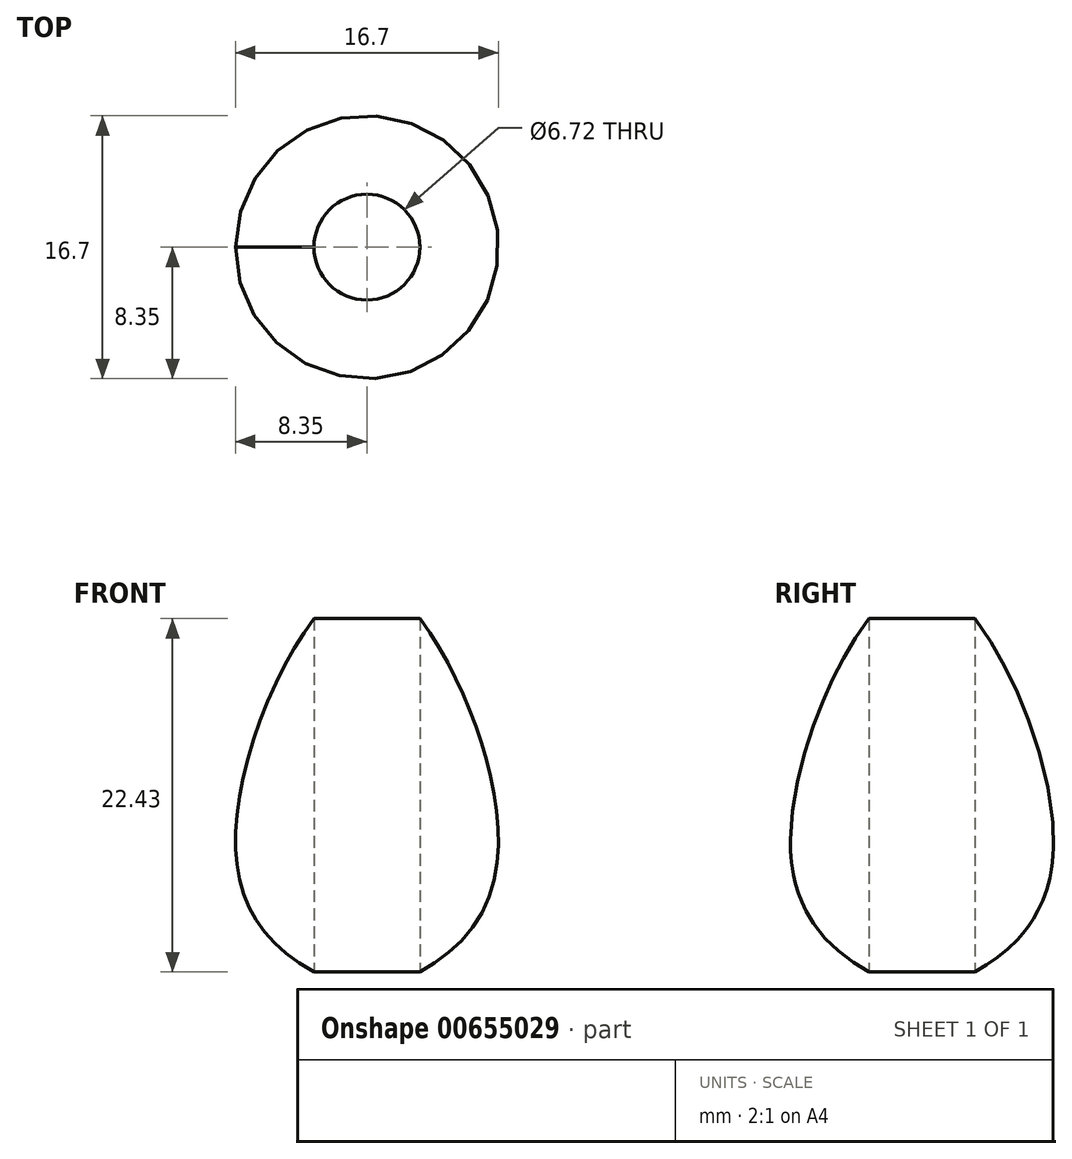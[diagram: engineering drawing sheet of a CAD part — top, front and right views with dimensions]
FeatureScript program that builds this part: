
annotation { "Feature Type Name" : "Feature", "Feature Type Description" : "" }
export const myFeature = defineFeature(function(context is Context, id is Id, definition is map)
    precondition{}
    {
        {
            var Q0;
            Q0=qCreatedBy(makeId("Front.planeOp"),FACE);
            var sketch = newSketch(context, id + "F0", { "sketchPlane" : qUnion([Q0])});
            skLineSegment(sketch, "E0", {"start": v(0, 0) * mm, "end": v(0, 26.69) * mm});
            skFitSpline(sketch, "E1", {"points": [v(0, 26.69) * mm, v(8.32, 10.8) * mm, v(0, 0) * mm], "startDerivative": vector(21.04, -7) * mm, "endDerivative": vector(-40.49, -13.21) * mm});
            skSolve(sketch);
        }
        {
            var Q0;
            Q0=makeQuery(id+"F0.imprint","IMPRINT",FACE,{"disambiguationData":[TD([[makeQuery(id+"F0.imprint","IMPRINT",EDGE,{"derivedFrom":sQuery(id+"F0.wireOp",EDGE,"E0")}),-1.0]])]});
            var Q1;
            Q1=sQuery(id+"F0.wireOp",EDGE,"E0");
            revolve(context, id + "F1", {"entities" : qUnion([Q0]), "axis" : qUnion([Q1]), "revolveType" : RevolveType.FULL});
        }
        {
            var Q0;
            Q0=qCreatedBy(makeId("Top.planeOp"),FACE);
            var sketch = newSketch(context, id + "F2", { "sketchPlane" : qUnion([Q0])});
            skCircle(sketch, "E2", {"center": v(0, 0) * mm, "radius": 3.36 * mm});
            skSolve(sketch);
        }
        {
            var Q0;
            Q0 = qSketchRegion(id + "F2", true);
            extrude(context, id + "F3", {"entities" : qUnion([Q0]), "operationType" : NewBodyOperationType.REMOVE, "endBound" : BoundingType.THROUGH_ALL, "depth" : 25.4 * mm, "offsetDistance" : 25.4 * mm});
        }
    });
